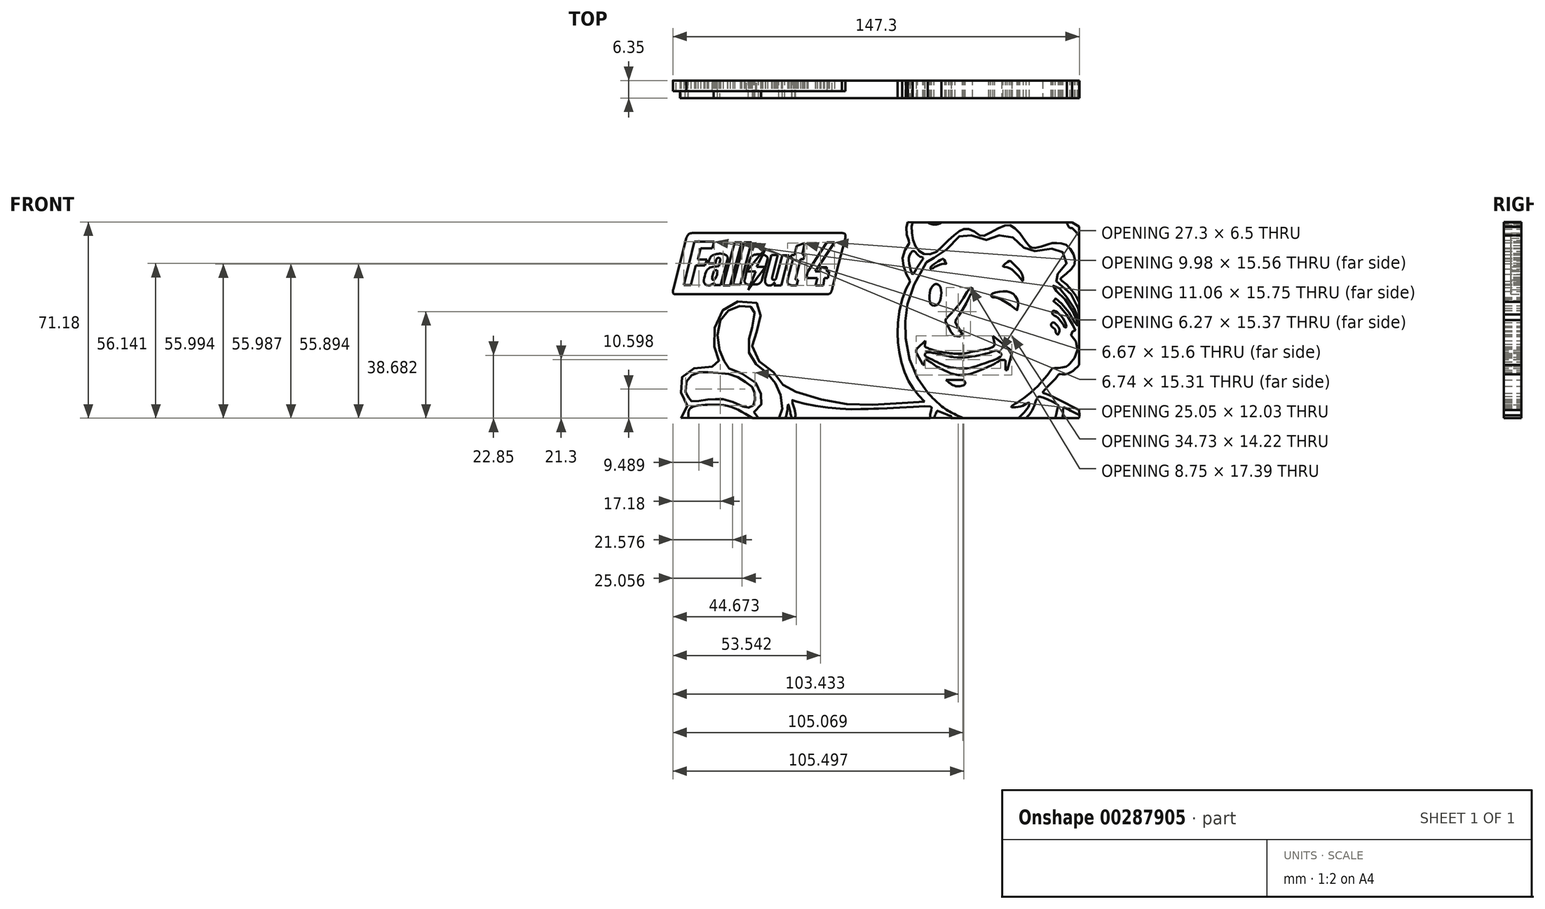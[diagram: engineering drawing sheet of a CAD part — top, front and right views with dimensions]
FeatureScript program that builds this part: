
annotation { "Feature Type Name" : "Feature", "Feature Type Description" : "" }
export const myFeature = defineFeature(function(context is Context, id is Id, definition is map)
    precondition{}
    {
        {
            var Q0;
            Q0=qCreatedBy(makeId("Front.planeOp"),FACE);
            var sketch = newSketch(context, id + "F0", { "sketchPlane" : qUnion([Q0])});
            skLineSegment(sketch, "E0", {"start": v(-63.85, 33.57) * mm, "end": v(-56.67, 33.57) * mm});
            skLineSegment(sketch, "E1", {"start": v(-56.67, 33.57) * mm, "end": v(-57.4, 31.22) * mm});
            skLineSegment(sketch, "E2", {"start": v(-57.4, 31.22) * mm, "end": v(-61.58, 31.22) * mm});
            skLineSegment(sketch, "E3", {"start": v(-61.58, 31.22) * mm, "end": v(-62.68, 27.12) * mm});
            skLineSegment(sketch, "E4", {"start": v(-62.68, 27.12) * mm, "end": v(-59.3, 27.12) * mm});
            skLineSegment(sketch, "E5", {"start": v(-59.3, 27.12) * mm, "end": v(-60.11, 24.92) * mm});
            skLineSegment(sketch, "E6", {"start": v(-60.11, 24.92) * mm, "end": v(-63.4, 24.92) * mm});
            skLineSegment(sketch, "E7", {"start": v(-63.4, 24.92) * mm, "end": v(-65.24, 17.82) * mm});
            skLineSegment(sketch, "E8", {"start": v(-65.24, 17.82) * mm, "end": v(-67.73, 17.82) * mm});
            skLineSegment(sketch, "E9", {"start": v(-67.73, 17.82) * mm, "end": v(-63.85, 33.57) * mm});
            skLineSegment(sketch, "E10", {"start": v(-49.34, 33.35) * mm, "end": v(-46.78, 33.35) * mm});
            skLineSegment(sketch, "E11", {"start": v(-46.78, 33.35) * mm, "end": v(-50.96, 17.74) * mm});
            skLineSegment(sketch, "E12", {"start": v(-50.96, 17.74) * mm, "end": v(-53.45, 17.74) * mm});
            skLineSegment(sketch, "E13", {"start": v(-53.45, 17.74) * mm, "end": v(-49.34, 33.35) * mm});
            skLineSegment(sketch, "E14", {"start": v(-45.9, 33.35) * mm, "end": v(-43.26, 33.35) * mm});
            skLineSegment(sketch, "E15", {"start": v(-43.26, 33.35) * mm, "end": v(-47.22, 18.04) * mm});
            skLineSegment(sketch, "E16", {"start": v(-47.22, 18.04) * mm, "end": v(-50, 18.04) * mm});
            skLineSegment(sketch, "E17", {"start": v(-50, 18.04) * mm, "end": v(-45.9, 33.35) * mm});
            skPoint(sketch, "E18.13.internal.orphan", {"position": v(-38.14, 18.1) * mm});
            skPoint(sketch, "E18.14.internal.orphan", {"position": v(-38.14, 20.67) * mm});
            skPoint(sketch, "E18.15.internal.orphan", {"position": v(-37.04, 24.48) * mm});
            skPoint(sketch, "E19.start.orphan", {"position": v(-23.14, 20.54) * mm});
            skPoint(sketch, "E20.start.orphan", {"position": v(-16.58, 20.54) * mm});
            skLineSegment(sketch, "E21", {"start": v(-35.93, 28.79) * mm, "end": v(-33.7, 28.79) * mm});
            skLineSegment(sketch, "E22", {"start": v(-33.7, 28.79) * mm, "end": v(-35.76, 20.65) * mm});
            skLineSegment(sketch, "E23", {"start": v(-29.6, 28.68) * mm, "end": v(-31.98, 28.68) * mm});
            skLineSegment(sketch, "E24", {"start": v(-31.98, 28.68) * mm, "end": v(-34.2, 20.7) * mm});
            skLineSegment(sketch, "E25", {"start": v(-35.93, 28.79) * mm, "end": v(-38.14, 20.67) * mm});
            skLineSegment(sketch, "E26", {"start": v(-29.6, 28.68) * mm, "end": v(-32.36, 17.79) * mm});
            skLineSegment(sketch, "E27", {"start": v(-32.36, 17.79) * mm, "end": v(-35.03, 17.79) * mm});
            skFitSpline(sketch, "E28", {"points": [v(-35.76, 20.65) * mm, v(-35.65, 19.94) * mm, v(-34.99, 19.79) * mm, v(-34.43, 20) * mm, v(-34.2, 20.7) * mm], "startDerivative": vector(-0.16, -3.28) * mm, "endDerivative": vector(0.54, 3.14) * mm});
            skLineSegment(sketch, "E29", {"start": v(-35.03, 17.79) * mm, "end": v(-34.72, 18.75) * mm});
            skFitSpline(sketch, "E30", {"points": [v(-34.72, 18.75) * mm, v(-34.94, 18.75) * mm, v(-35.56, 18.07) * mm, v(-37.05, 17.76) * mm, v(-38.15, 18.56) * mm, v(-38.14, 20.67) * mm], "startDerivative": vector(-2.4, 0.72) * mm, "endDerivative": vector(1.34, 8.58) * mm});
            skLineSegment(sketch, "E31", {"start": v(-23.88, 33.13) * mm, "end": v(-26.81, 32.04) * mm});
            skLineSegment(sketch, "E32", {"start": v(-26.81, 32.04) * mm, "end": v(-27.54, 28.79) * mm});
            skLineSegment(sketch, "E33", {"start": v(-27.54, 28.79) * mm, "end": v(-28.74, 28.79) * mm});
            skLineSegment(sketch, "E34", {"start": v(-28.74, 28.79) * mm, "end": v(-28.96, 27.47) * mm});
            skLineSegment(sketch, "E35", {"start": v(-28.96, 27.47) * mm, "end": v(-28.06, 27.47) * mm});
            skLineSegment(sketch, "E36", {"start": v(-28.06, 27.47) * mm, "end": v(-29.95, 20.3) * mm});
            skLineSegment(sketch, "E37", {"start": v(-23.88, 33.13) * mm, "end": v(-24.83, 28.97) * mm});
            skLineSegment(sketch, "E38", {"start": v(-24.83, 28.97) * mm, "end": v(-23.88, 28.97) * mm});
            skLineSegment(sketch, "E39", {"start": v(-23.88, 28.97) * mm, "end": v(-24.23, 27.33) * mm});
            skLineSegment(sketch, "E40", {"start": v(-24.23, 27.33) * mm, "end": v(-25.41, 27.33) * mm});
            skLineSegment(sketch, "E41", {"start": v(-25.41, 27.33) * mm, "end": v(-27.09, 20.63) * mm});
            skFitSpline(sketch, "E42", {"points": [v(-27.09, 20.63) * mm, v(-27.09, 19.84) * mm, v(-26.27, 19.84) * mm], "startDerivative": vector(-0.4, -2) * mm, "endDerivative": vector(2.04, 0.4) * mm});
            skLineSegment(sketch, "E43", {"start": v(-26.27, 19.84) * mm, "end": v(-26.8, 17.83) * mm});
            skFitSpline(sketch, "E44", {"points": [v(-29.95, 20.3) * mm, v(-30.1, 18.74) * mm, v(-29.18, 17.9) * mm, v(-26.8, 17.83) * mm], "startDerivative": vector(-1.34, -5.23) * mm, "endDerivative": vector(6.63, 0.57) * mm});
            skLineSegment(sketch, "E45", {"start": v(-15.88, 33.32) * mm, "end": v(-13.16, 33.32) * mm});
            skLineSegment(sketch, "E46", {"start": v(-13.16, 33.32) * mm, "end": v(-20.15, 22.87) * mm});
            skLineSegment(sketch, "E47", {"start": v(-20.15, 22.87) * mm, "end": v(-18.48, 22.87) * mm});
            skLineSegment(sketch, "E48", {"start": v(-18.48, 22.87) * mm, "end": v(-18.12, 24.37) * mm});
            skLineSegment(sketch, "E49", {"start": v(-18.12, 24.37) * mm, "end": v(-15.92, 24.37) * mm});
            skLineSegment(sketch, "E50", {"start": v(-15.92, 22.87) * mm, "end": v(-15.03, 22.87) * mm});
            skLineSegment(sketch, "E51", {"start": v(-15.03, 22.87) * mm, "end": v(-15.53, 20.37) * mm});
            skLineSegment(sketch, "E52", {"start": v(-15.53, 20.37) * mm, "end": v(-16.78, 20.37) * mm});
            skLineSegment(sketch, "E53", {"start": v(-16.78, 20.37) * mm, "end": v(-17.14, 17.76) * mm});
            skLineSegment(sketch, "E54", {"start": v(-17.14, 17.76) * mm, "end": v(-20, 17.76) * mm});
            skLineSegment(sketch, "E55", {"start": v(-20, 17.76) * mm, "end": v(-19.27, 20.37) * mm});
            skLineSegment(sketch, "E56", {"start": v(-19.27, 20.37) * mm, "end": v(-23.14, 20.37) * mm});
            skLineSegment(sketch, "E57", {"start": v(-23.14, 20.37) * mm, "end": v(-23.14, 21.57) * mm});
            skLineSegment(sketch, "E58", {"start": v(-22.78, 22.87) * mm, "end": v(-15.88, 33.32) * mm});
            skLineSegment(sketch, "E59", {"start": v(-22.78, 22.87) * mm, "end": v(-23.14, 21.57) * mm});
            skLineSegment(sketch, "E60", {"start": v(-15.92, 24.37) * mm, "end": v(-15.92, 22.87) * mm});
            skPoint(sketch, "E61.10.internal.orphan", {"position": v(-71.53, 16.13) * mm});
            skPoint(sketch, "E62.10.internal.orphan", {"position": v(-38.14, 28.8) * mm});
            skPoint(sketch, "E62.5.internal.orphan", {"position": v(-44.95, 18.18) * mm});
            skLineSegment(sketch, "E63", {"start": v(-54.48, 27.02) * mm, "end": v(-55, 24.67) * mm});
            skLineSegment(sketch, "E64", {"start": v(-52.02, 26.91) * mm, "end": v(-54.39, 17.91) * mm});
            skLineSegment(sketch, "E65", {"start": v(-54.39, 17.91) * mm, "end": v(-56.84, 17.91) * mm});
            skLineSegment(sketch, "E66", {"start": v(-56.84, 17.91) * mm, "end": v(-56.65, 18.62) * mm});
            skLineSegment(sketch, "E67", {"start": v(-56.26, 25.8) * mm, "end": v(-58.83, 25.8) * mm});
            skLineSegment(sketch, "E68", {"start": v(-56.26, 25.8) * mm, "end": v(-56.02, 26.9) * mm});
            skFitSpline(sketch, "E69", {"points": [v(-56.02, 26.9) * mm, v(-55.64, 27.6) * mm, v(-54.92, 27.7) * mm, v(-54.52, 27.38) * mm, v(-54.48, 27.02) * mm], "startDerivative": vector(0.9, 2.82) * mm, "endDerivative": vector(-0.12, -1.87) * mm});
            skFitSpline(sketch, "E70", {"points": [v(-58.83, 25.8) * mm, v(-58.07, 28) * mm, v(-57.05, 28.76) * mm, v(-55.57, 29.2) * mm, v(-53.5, 29.16) * mm, v(-51.91, 28.14) * mm, v(-52.02, 26.91) * mm], "startDerivative": vector(3.07, 12.97) * mm, "endDerivative": vector(-2.97, -9.05) * mm});
            skFitSpline(sketch, "E71", {"points": [v(-56.65, 18.62) * mm, v(-57.35, 18.23) * mm, v(-58.4, 17.73) * mm, v(-59.8, 17.98) * mm, v(-60.42, 18.86) * mm, v(-60.16, 21.18) * mm, v(-59.46, 23.12) * mm, v(-58.54, 24.03) * mm, v(-57.42, 24.5) * mm, v(-55, 24.67) * mm], "startDerivative": vector(-8.34, -4.38) * mm, "endDerivative": vector(18.81, 0.4) * mm});
            skFitSpline(sketch, "E72", {"points": [v(-55.8, 23.29) * mm, v(-56.65, 23.05) * mm, v(-57.18, 21.9) * mm, v(-57.48, 20.39) * mm, v(-57.29, 19.76) * mm, v(-56.65, 19.9) * mm, v(-56.1, 20.6) * mm, v(-55.6, 22.31) * mm, v(-55.8, 23.29) * mm]});
            skPoint(sketch, "E73.orphan", {"position": v(-38.14, 31) * mm});
            skPoint(sketch, "E74.end.orphan", {"position": v(-44.36, 16.13) * mm});
            skPoint(sketch, "E75.start.orphan", {"position": v(-44.95, 22.8) * mm});
            skPoint(sketch, "E76.2.internal.orphan", {"position": v(-43.57, 18.18) * mm});
            skPoint(sketch, "E77.start.orphan", {"position": v(-38.14, 24.48) * mm});
            skLineSegment(sketch, "E78", {"start": v(-44.95, 22.8) * mm, "end": v(-41.74, 22.8) * mm});
            skLineSegment(sketch, "E79", {"start": v(-41.74, 22.8) * mm, "end": v(-43.72, 17.78) * mm});
            skLineSegment(sketch, "E80", {"start": v(-41.35, 24.5) * mm, "end": v(-38.14, 24.48) * mm});
            skLineSegment(sketch, "E81", {"start": v(-38.14, 24.48) * mm, "end": v(-44.36, 16.13) * mm});
            skLineSegment(sketch, "E82", {"start": v(-43.72, 17.78) * mm, "end": v(-44.36, 16.13) * mm});
            skPoint(sketch, "E83.start.orphan", {"position": v(-38.14, 30.6) * mm});
            skLineSegment(sketch, "E84", {"start": v(-41.35, 24.5) * mm, "end": v(-38.14, 31) * mm});
            skLineSegment(sketch, "E85", {"start": v(-39.77, 29.18) * mm, "end": v(-44.95, 22.8) * mm});
            skLineSegment(sketch, "E86", {"start": v(-39.77, 29.18) * mm, "end": v(-38.14, 31) * mm});
            skLineSegment(sketch, "E87", {"start": v(-44.95, 22.8) * mm, "end": v(-43.87, 27) * mm});
            skFitSpline(sketch, "E88", {"points": [v(-43.87, 27) * mm, v(-43.47, 27.97) * mm, v(-42.78, 28.55) * mm, v(-41.95, 28.9) * mm, v(-40.62, 29.08) * mm, v(-39.85, 29.07) * mm], "startDerivative": vector(1.5, 5.13) * mm, "endDerivative": vector(3.94, -0.22) * mm});
            skLineSegment(sketch, "E89", {"start": v(-38.14, 24.48) * mm, "end": v(-37.38, 27.31) * mm});
            skFitSpline(sketch, "E90", {"points": [v(-37.38, 27.31) * mm, v(-37.38, 27.8) * mm, v(-37.74, 28.26) * mm, v(-38.35, 28.69) * mm, v(-39.15, 28.96) * mm], "startDerivative": vector(0.35, 2.35) * mm, "endDerivative": vector(-2.93, 0.81) * mm});
            skLineSegment(sketch, "E91", {"start": v(-38.14, 24.48) * mm, "end": v(-39.5, 19.4) * mm});
            skFitSpline(sketch, "E92", {"points": [v(-39.5, 19.4) * mm, v(-40.02, 18.78) * mm, v(-40.6, 18.3) * mm, v(-41.79, 18.1) * mm, v(-42.9, 18.1) * mm], "startDerivative": vector(-2.27, -2.74) * mm, "endDerivative": vector(-3.97, 0.04) * mm});
            skLineSegment(sketch, "E93", {"start": v(-44.95, 22.8) * mm, "end": v(-45.68, 19.95) * mm});
            skFitSpline(sketch, "E94", {"points": [v(-45.68, 19.95) * mm, v(-45.68, 18.94) * mm, v(-44.95, 18.18) * mm, v(-43.6, 18.06) * mm], "startDerivative": vector(-0.5, -3.29) * mm, "endDerivative": vector(3.92, 0.17) * mm});
            skSolve(sketch);
        }
        {
            var Q0;
            Q0=qCreatedBy(makeId("Front.planeOp"),FACE);
            var sketch = newSketch(context, id + "F1", { "sketchPlane" : qUnion([Q0])});
            skLineSegment(sketch, "E95", {"start": v(-63.81, 36.77) * mm, "end": v(-12.41, 36.77) * mm});
            skLineSegment(sketch, "E96", {"start": v(-9.4, 34.04) * mm, "end": v(-13.7, 17.53) * mm});
            skLineSegment(sketch, "E97", {"start": v(-17.3, 14.51) * mm, "end": v(-68.84, 14.51) * mm});
            skLineSegment(sketch, "E98", {"start": v(-66.83, 34.9) * mm, "end": v(-71.57, 16.38) * mm});
            skFitSpline(sketch, "E99", {"points": [v(-66.83, 34.9) * mm, v(-65.9, 36.4) * mm, v(-63.81, 36.77) * mm], "startDerivative": vector(1.47, 3.75) * mm, "endDerivative": vector(4.51, 0.04) * mm});
            skLineSegment(sketch, "E100", {"start": v(-68.84, 14.51) * mm, "end": v(-70.55, 14.51) * mm});
            skFitSpline(sketch, "E101", {"points": [v(-70.55, 14.51) * mm, v(-71.44, 14.72) * mm, v(-71.69, 15.6) * mm, v(-71.57, 16.38) * mm], "startDerivative": vector(-3.02, 0.07) * mm, "endDerivative": vector(0.56, 2.28) * mm});
            skLineSegment(sketch, "E102", {"start": v(-17.3, 14.51) * mm, "end": v(-15.8, 14.51) * mm});
            skLineSegment(sketch, "E103", {"start": v(-13.7, 17.53) * mm, "end": v(-14.05, 16.18) * mm});
            skFitSpline(sketch, "E104", {"points": [v(-14.05, 16.18) * mm, v(-14.63, 14.9) * mm, v(-15.8, 14.51) * mm], "startDerivative": vector(-0.8, -2.88) * mm, "endDerivative": vector(-2.72, -0.42) * mm});
            skLineSegment(sketch, "E105", {"start": v(-12.41, 36.77) * mm, "end": v(-10.38, 36.77) * mm});
            skFitSpline(sketch, "E106", {"points": [v(-9.4, 34.04) * mm, v(-9.14, 35.44) * mm, v(-9.4, 36.48) * mm, v(-10.38, 36.77) * mm], "startDerivative": vector(0.97, 3.8) * mm, "endDerivative": vector(-3.67, 0.34) * mm});
            skSolve(sketch);
        }
        {
            var Q0;
            Q0 = qSketchRegion(id + "F1", true);
            extrude(context, id + "F2", {"entities" : qUnion([Q0]), "depth" : 3.8 * mm});
        }
        {
            var Q0;
            Q0 = qSketchRegion(id + "F0", true);
            extrude(context, id + "F3", {"entities" : qUnion([Q0]), "operationType" : NewBodyOperationType.REMOVE, "oppositeDirection" : true, "depth" : 50.8 * mm, "hasSecondDirection" : true, "secondDirectionOppositeDirection" : false, "secondDirectionDepth" : 50.8 * mm});
        }
        {
            var Q0;
            {var subQ0=sQuery(id+"F0.wireOp",EDGE,"E87");Q0=makeQuery(id+"F0.imprint","IMPRINT",FACE,{"disambiguationData":[TD([[makeQuery(id+"F0.imprint","IMPRINT",EDGE,{"derivedFrom":subQ0}),-1.0]])]});}
            var Q1;
            {var subQ0=sQuery(id+"F0.wireOp",EDGE,"E80");Q1=makeQuery(id+"F0.imprint","IMPRINT",FACE,{"disambiguationData":[TD([[makeQuery(id+"F0.imprint","IMPRINT",EDGE,{"derivedFrom":subQ0}),1.0]])]});}
            var Q2;
            {var subQ0=sQuery(id+"F0.wireOp",EDGE,"E78");Q2=makeQuery(id+"F0.imprint","IMPRINT",FACE,{"disambiguationData":[TD([[makeQuery(id+"F0.imprint","IMPRINT",EDGE,{"derivedFrom":subQ0}),-1.0]])]});}
            var Q3;
            {var subQ0=sQuery(id+"F0.wireOp",EDGE,"E91");Q3=makeQuery(id+"F0.imprint","IMPRINT",FACE,{"disambiguationData":[TD([[makeQuery(id+"F0.imprint","IMPRINT",EDGE,{"derivedFrom":subQ0}),-1.0]])]});}
            extrude(context, id + "F4", {"entities" : qUnion([Q0, Q1, Q2, Q3]), "depth" : 3.8 * mm});
        }
        {
            var Q0;
            Q0=qCreatedBy(makeId("Front.planeOp"),FACE);
            var sketch = newSketch(context, id + "F5", { "sketchPlane" : qUnion([Q0])});
            skFitSpline(sketch, "E107", {"points": [v(-68.68, -30.34) * mm, v(-68.33, -27.94) * mm, v(-66.38, -25.59) * mm, v(-67.92, -23.03) * mm, v(-69.04, -19.55) * mm, v(-68.63, -16.07) * mm, v(-66.9, -13.82) * mm, v(-64.03, -12.3) * mm, v(-59.02, -11.68) * mm, v(-55.85, -11.68) * mm, v(-54.73, -10.65) * mm, v(-55.34, -8.81) * mm, v(-56.36, -5.75) * mm, v(-56.87, -1.96) * mm, v(-56.26, 3.77) * mm, v(-54.01, 8.27) * mm, v(-50.64, 11.13) * mm, v(-46.03, 12.15) * mm, v(-41.23, 11.33) * mm, v(-40, 9.29) * mm, v(-39.9, 6.32) * mm, v(-40.82, 2.64) * mm, v(-42.15, -1.04) * mm, v(-42.97, -3.6) * mm, v(-41.64, -8.3) * mm, v(-39.7, -10.35) * mm, v(-35.6, -13.42) * mm, v(-32.84, -16.18) * mm, v(-31.72, -18.53) * mm, v(-31.4, -18.84) * mm, v(-26.8, -20.98) * mm, v(-17.2, -23.85) * mm, v(-8.3, -25.38) * mm, v(1.11, -25.59) * mm, v(13.08, -24.87) * mm, v(19.52, -24.46) * mm], "startDerivative": vector(-9.45, 112.44) * mm, "endDerivative": vector(162.37, 9.81) * mm});
            skFitSpline(sketch, "E108", {"points": [v(19.52, -24.46) * mm, v(15.37, -19.6) * mm, v(12, -12.77) * mm, v(10, -3.93) * mm, v(9.9, 4.17) * mm, v(12.45, 15.65) * mm, v(14.36, 19.57) * mm, v(14.02, 19.83) * mm, v(12.12, 23.96) * mm, v(11.87, 29.38) * mm, v(14.19, 33.5) * mm, v(13.76, 34.02) * mm, v(12.81, 38.06) * mm, v(13.41, 40.73) * mm], "startDerivative": vector(-49.03, 51.65) * mm, "endDerivative": vector(15.36, 39.31) * mm});
            skFitSpline(sketch, "E109", {"points": [v(73.02, 40.63) * mm, v(75.51, 39.11) * mm], "startDerivative": vector(2.5, -1.52) * mm, "endDerivative": vector(2.5, -1.52) * mm});
            skFitSpline(sketch, "E110", {"points": [v(75.51, -11.1) * mm, v(73.4, -13.16) * mm, v(70.34, -14.47) * mm, v(68.27, -14.47) * mm, v(67.35, -15.7) * mm, v(62.37, -20.98) * mm, v(62.91, -21.36) * mm, v(75.51, -27.49) * mm], "startDerivative": vector(-14.96, -17) * mm, "endDerivative": vector(58.28, -29.89) * mm});
            skFitSpline(sketch, "E111", {"points": [v(-66, -30.3) * mm, v(-65.9, -27.49) * mm, v(-64.5, -26.28) * mm, v(-58.1, -25.52) * mm, v(-50.73, -26.28) * mm, v(-42.82, -30.4) * mm], "startDerivative": vector(-1.53, 21.1) * mm, "endDerivative": vector(29.91, -18.64) * mm});
            skFitSpline(sketch, "E112", {"points": [v(-40.64, -30.38) * mm, v(-42.46, -28.37) * mm, v(-42.1, -28.1) * mm, v(-39.64, -25.28) * mm, v(-39.64, -22) * mm, v(-41.46, -17.71) * mm, v(-48.2, -13.52) * mm, v(-52.12, -11.8) * mm, v(-53.12, -9.51) * mm, v(-54.85, -5.5) * mm, v(-55.4, 1.6) * mm, v(-53.3, 7.07) * mm, v(-49.57, 9.62) * mm, v(-45.29, 10.35) * mm, v(-42.55, 9.53) * mm, v(-42.1, 8.25) * mm, v(-43.1, 2.15) * mm, v(-44.1, -1.95) * mm, v(-43.83, -7.78) * mm, v(-40.18, -11.97) * mm, v(-36, -15.7) * mm, v(-33.35, -20.17) * mm, v(-31.98, -25.37) * mm, v(-32.8, -29.74) * mm, v(-33.26, -30.38) * mm], "startDerivative": vector(-79.5, 75.35) * mm, "endDerivative": vector(-24.05, -24.57) * mm});
            skFitSpline(sketch, "E113", {"points": [v(-31.4, -30.53) * mm, v(-30.65, -29.74) * mm, v(-29.88, -25.49) * mm, v(-29.4, -27.3) * mm, v(-28.55, -30.4) * mm], "startDerivative": vector(4.95, 2.02) * mm, "endDerivative": vector(3.13, -10.02) * mm});
            skFitSpline(sketch, "E114", {"points": [v(-64.91, -24.35) * mm, v(-60.79, -23.88) * mm, v(-56.43, -23.53) * mm, v(-51.72, -23.94) * mm, v(-45.06, -26.65) * mm, v(-44, -26.53) * mm, v(-42.3, -25.41) * mm, v(-41.94, -22.76) * mm, v(-42.4, -19.93) * mm, v(-45.6, -17.1) * mm, v(-50.9, -14.45) * mm, v(-58.26, -13.87) * mm, v(-63.32, -13.98) * mm, v(-66.56, -16.87) * mm, v(-66.97, -18.84) * mm, v(-67.1, -20.98) * mm, v(-65.85, -23.23) * mm, v(-64.91, -24.35) * mm]});
            skFitSpline(sketch, "E115", {"points": [v(-27.42, -30.4) * mm, v(-27.25, -28.71) * mm, v(-28.53, -24.02) * mm, v(-27.33, -24.24) * mm, v(-11.4, -26.99) * mm, v(0, -27.02) * mm, v(4.79, -26.92) * mm, v(21.57, -26.2) * mm, v(21.84, -26.38) * mm, v(22.11, -26.65) * mm, v(21.63, -28.3) * mm, v(21.56, -30.4) * mm], "startDerivative": vector(8.2, 21.52) * mm, "endDerivative": vector(3, -31.74) * mm});
            skFitSpline(sketch, "E116", {"points": [v(22.99, -30.32) * mm, v(24.15, -27.74) * mm, v(24.7, -27.91) * mm, v(29.13, -29.72) * mm, v(29.18, -29.8) * mm, v(29, -30.36) * mm], "startDerivative": vector(4.51, 12.02) * mm, "endDerivative": vector(-1.67, -5.2) * mm});
            skFitSpline(sketch, "E117", {"points": [v(66.9, -30.35) * mm, v(68, -25.83) * mm, v(67.97, -25.64) * mm, v(61.19, -22.53) * mm, v(60.65, -22.8) * mm, v(60.08, -23.5) * mm, v(59.54, -25.3) * mm, v(58.12, -28.2) * mm, v(56.36, -30.42) * mm], "startDerivative": vector(7.82, 33.75) * mm, "endDerivative": vector(-12.8, -14.65) * mm});
            skFitSpline(sketch, "E118", {"points": [v(75.6, -29.31) * mm, v(70.13, -26.51) * mm, v(70.05, -26.51) * mm, v(69.72, -27.24) * mm, v(69.68, -29.31) * mm, v(69.28, -30.45) * mm], "startDerivative": vector(-19.13, 9.91) * mm, "endDerivative": vector(-3, -5.65) * mm});
            skFitSpline(sketch, "E119", {"points": [v(33.9, -30.45) * mm, v(29.65, -28.58) * mm, v(25.47, -25.88) * mm, v(20.83, -21.43) * mm], "startDerivative": vector(-13.82, 5.6) * mm, "endDerivative": vector(-12.63, 13.03) * mm});
            skFitSpline(sketch, "E120", {"points": [v(20.83, -21.43) * mm, v(17.6, -16.99) * mm, v(14.9, -11.5) * mm, v(12.9, -3.9) * mm, v(12.58, 1.63) * mm, v(12.66, 5.95) * mm, v(13.26, 10.63) * mm, v(15.09, 16.65) * mm, v(20.01, 25.83) * mm, v(21.3, 27.62) * mm, v(21.53, 27.62) * mm, v(23.81, 28.12) * mm, v(26.68, 30.08) * mm, v(30.69, 34.04) * mm, v(33.29, 36.4) * mm, v(35.8, 36.27) * mm, v(39.3, 34.4) * mm, v(43.21, 34.5) * mm, v(46.04, 35.73) * mm, v(47.9, 36.05) * mm, v(51.69, 35.05) * mm, v(54.83, 32.45) * mm, v(56.01, 30.76) * mm, v(57.96, 30.1) * mm, v(62.94, 30.84) * mm, v(66.29, 31.05) * mm, v(68.47, 30.73) * mm, v(70.2, 29) * mm, v(71.02, 26.9) * mm, v(70.52, 24.45) * mm, v(68.1, 22.08) * mm, v(66.28, 20.94) * mm, v(66.55, 19.85) * mm, v(70.15, 17.07) * mm, v(74.34, 11.97) * mm, v(75.13, 9.54) * mm], "startDerivative": vector(-94.55, 122.24) * mm, "endDerivative": vector(18.57, -91.09) * mm});
            skFitSpline(sketch, "E121", {"points": [v(75.13, 9.54) * mm, v(75.57, 7.15) * mm], "startDerivative": vector(0.43, -2.4) * mm, "endDerivative": vector(0.43, -2.4) * mm});
            skFitSpline(sketch, "E122", {"points": [v(75.54, 5.23) * mm, v(73.01, 10.67) * mm, v(69.97, 14.93) * mm, v(67.39, 17.67) * mm, v(66.17, 17.67) * mm, v(66.17, 16.78) * mm, v(68.27, 14.9) * mm, v(72.16, 10.28) * mm, v(74.29, 5.93) * mm, v(74.98, 4.38) * mm, v(74.98, 3.44) * mm, v(74.6, 2.95) * mm, v(74.02, 3.98) * mm, v(72.16, 7.6) * mm, v(69.24, 11.16) * mm, v(67.33, 12.83) * mm, v(66.57, 13.1) * mm, v(66.08, 12.74) * mm, v(66.69, 11.52) * mm, v(68.8, 9.86) * mm, v(71.15, 6.9) * mm, v(73.64, 2.74) * mm, v(74.05, 1.95) * mm, v(74.02, 1.37) * mm, v(73.15, 1.34) * mm, v(73.24, 1.05) * mm, v(72.34, 0.95) * mm, v(72.4, 0) * mm, v(73.85, -1.6) * mm, v(74.74, -3.74) * mm, v(74.74, -6.51) * mm, v(73.9, -8.54) * mm], "startDerivative": vector(-42.47, 103.93) * mm, "endDerivative": vector(-30.71, -57.47) * mm});
            skFitSpline(sketch, "E123", {"points": [v(73.9, -8.54) * mm, v(72.4, -10.37) * mm, v(70.34, -11.82) * mm, v(65.67, -12.4) * mm, v(65.6, -12.54) * mm, v(61.62, -17.6) * mm, v(54.97, -23.53) * mm, v(51.36, -25.77) * mm], "startDerivative": vector(-13.26, -16.22) * mm, "endDerivative": vector(-21.89, -12.39) * mm});
            skFitSpline(sketch, "E124", {"points": [v(51.36, -25.77) * mm, v(50.96, -26.26) * mm, v(51.36, -26.47) * mm, v(55.32, -25.77) * mm, v(57.4, -24.83) * mm, v(57.2, -26.16) * mm, v(53.52, -30.4) * mm], "startDerivative": vector(-6.4, -5.89) * mm, "endDerivative": vector(-16.44, -15.88) * mm});
            skFitSpline(sketch, "E125", {"points": [v(65.37, 3.22) * mm, v(66.82, 1.82) * mm, v(67.15, 0.52) * mm, v(67.88, 0) * mm, v(68.31, 1) * mm, v(68.31, 2.16) * mm, v(66.59, 4.14) * mm, v(65.8, 4.24) * mm, v(65.37, 3.22) * mm]});
            skFitSpline(sketch, "E126", {"points": [v(68.06, 5.76) * mm, v(69.3, 4.3) * mm, v(70.5, 2.55) * mm, v(70.82, 2.55) * mm, v(70.84, 3.5) * mm, v(69.3, 6.3) * mm, v(67.06, 8.37) * mm, v(66, 8.43) * mm, v(65.8, 7.51) * mm, v(67.51, 6.25) * mm, v(68.06, 5.76) * mm]});
            skFitSpline(sketch, "E127", {"points": [v(19.07, 27.84) * mm, v(16.98, 24.58) * mm, v(15.31, 21.84) * mm, v(14.16, 24.66) * mm, v(13.94, 28.13) * mm, v(15.31, 30.23) * mm, v(16.47, 29.57) * mm, v(17.7, 28.27) * mm, v(19.07, 27.84) * mm]});
            skFitSpline(sketch, "E128", {"points": [v(15.27, 40.58) * mm, v(14.84, 39.55) * mm, v(15, 36.08) * mm, v(15.98, 32.45) * mm, v(17.76, 29.96) * mm, v(19.88, 29.04) * mm, v(23.23, 29.58) * mm, v(27.14, 33.05) * mm, v(30.5, 36.24) * mm, v(32.93, 37.87) * mm, v(34.61, 38.25) * mm, v(36.94, 37.6) * mm, v(39.76, 35.8) * mm, v(41.33, 35.8) * mm, v(45.99, 38.3) * mm, v(49.46, 39.65) * mm, v(51.46, 39.17) * mm, v(54.06, 36.62) * mm], "startDerivative": vector(-14.62, -23.8) * mm, "endDerivative": vector(40.67, -46.63) * mm});
            skFitSpline(sketch, "E129", {"points": [v(54.06, 36.62) * mm, v(57.98, 31.63) * mm, v(58.21, 31.57) * mm, v(58.63, 31.36) * mm, v(62.75, 32.14) * mm, v(65.88, 33.07) * mm, v(68.13, 33.14) * mm, v(71.03, 32.34) * mm, v(73.45, 29.1) * mm, v(74.03, 26.01) * mm, v(72.24, 23.17) * mm, v(68.86, 20.41) * mm, v(68.77, 20.32) * mm, v(68.91, 19.7) * mm, v(69.68, 19.26) * mm, v(74.03, 14.53) * mm, v(75.04, 12.64) * mm], "startDerivative": vector(49.5, -68.91) * mm, "endDerivative": vector(10.4, -25.67) * mm});
            skFitSpline(sketch, "E130", {"points": [v(75.04, 12.64) * mm, v(75.6, 11.76) * mm], "startDerivative": vector(0.56, -0.88) * mm, "endDerivative": vector(0.56, -0.88) * mm});
            skFitSpline(sketch, "E131", {"points": [v(71.05, 40.61) * mm, v(71.56, 39.28) * mm, v(72.28, 38.62) * mm, v(73.15, 38.36) * mm, v(75.35, 36) * mm, v(75.6, 35.9) * mm], "startDerivative": vector(1.9, -6.47) * mm, "endDerivative": vector(1.99, -0.04) * mm});
            skFitSpline(sketch, "E132", {"points": [v(20.71, 40.55) * mm, v(22.1, 39.97) * mm, v(24.29, 39.97) * mm, v(25.67, 40.55) * mm], "startDerivative": vector(4.01, -2.2) * mm, "endDerivative": vector(4.01, 2.2) * mm});
            skFitSpline(sketch, "E133", {"points": [v(26.28, 27.39) * mm, v(27.34, 25.72) * mm, v(27.34, 25.58) * mm, v(25.36, 25.4) * mm, v(21.91, 23.77) * mm, v(21.57, 23.9) * mm, v(23.14, 25.65) * mm, v(25.8, 27.25) * mm, v(26.28, 27.39) * mm]});
            skFitSpline(sketch, "E134", {"points": [v(48.13, 25) * mm, v(50.22, 26.66) * mm, v(51.26, 26.03) * mm, v(55.07, 21.35) * mm, v(55.07, 19.34) * mm, v(54.67, 19.77) * mm, v(52.52, 22.3) * mm, v(50.08, 24.1) * mm, v(47.96, 24.68) * mm, v(48.13, 25) * mm]});
            skFitSpline(sketch, "E135", {"points": [v(43.6, 14.33) * mm, v(44.02, 13.53) * mm, v(44.89, 13.46) * mm, v(49.4, 11.43) * mm, v(53.1, 8.73) * mm, v(53.07, 8.86) * mm, v(53.52, 10.76) * mm, v(52.55, 13.66) * mm, v(50.04, 15.46) * mm, v(45.72, 15.3) * mm, v(43.6, 14.33) * mm]});
            skFitSpline(sketch, "E136", {"points": [v(22.96, 18.02) * mm, v(21.84, 16.6) * mm, v(21.32, 14.02) * mm, v(21.67, 11.14) * mm, v(23.17, 10.33) * mm, v(24.9, 11.62) * mm, v(25.58, 14.37) * mm, v(25.32, 16.86) * mm, v(24.5, 18.02) * mm, v(23.6, 18.24) * mm, v(22.96, 18.02) * mm]});
            skFitSpline(sketch, "E137", {"points": [v(36.12, 16.93) * mm, v(34, 13.79) * mm, v(31.4, 10.07) * mm, v(27.39, 5.68) * mm, v(26.95, 4.86) * mm, v(28.1, 2.98) * mm, v(29.56, 0) * mm, v(31.68, -0.84) * mm, v(33.23, 0) * mm, v(32.4, 1.34) * mm, v(31, 3.75) * mm, v(30.62, 4.67) * mm, v(31, 5.53) * mm, v(33.47, 9.2) * mm, v(36.02, 14.08) * mm, v(36.94, 16.2) * mm, v(36.84, 16.83) * mm, v(36.12, 16.93) * mm]});
            skLineSegment(sketch, "E138", {"start": v(27.32, -16.53) * mm, "end": v(33.46, -16.53) * mm});
            skFitSpline(sketch, "E139", {"points": [v(27.32, -16.53) * mm, v(27.8, -16.99) * mm, v(30.06, -18.54) * mm, v(33.22, -18.66) * mm, v(34.31, -17.63) * mm, v(33.46, -16.53) * mm], "startDerivative": vector(3.22, -3.07) * mm, "endDerivative": vector(-7.24, 6.1) * mm});
            skFitSpline(sketch, "E140", {"points": [v(29.56, -6.95) * mm, v(26.32, -6.54) * mm, v(22.64, -5.72) * mm, v(19.7, -4.5) * mm], "startDerivative": vector(-9.67, 1.08) * mm, "endDerivative": vector(-8.7, 4.12) * mm});
            skFitSpline(sketch, "E141", {"points": [v(29.56, -6.95) * mm, v(33.46, -6.95) * mm, v(38.13, -6.06) * mm, v(44.27, -4.56) * mm, v(44.96, -3.54) * mm], "startDerivative": vector(15.52, -0.77) * mm, "endDerivative": vector(2.28, 7.58) * mm});
            skLineSegment(sketch, "E142", {"start": v(19.77, -2.27) * mm, "end": v(19.7, -4.5) * mm});
            skLineSegment(sketch, "E143", {"start": v(19.77, -2.27) * mm, "end": v(16.94, -5) * mm});
            skLineSegment(sketch, "E144", {"start": v(44.96, -3.54) * mm, "end": v(44.34, -0.49) * mm});
            skLineSegment(sketch, "E145", {"start": v(44.34, -0.49) * mm, "end": v(50.22, -5.32) * mm});
            skFitSpline(sketch, "E146", {"points": [v(50.22, -5.32) * mm, v(51.13, -6.32) * mm, v(51.04, -7.41) * mm], "startDerivative": vector(2.24, -1.8) * mm, "endDerivative": vector(-0.65, -2.4) * mm});
            skLineSegment(sketch, "E147", {"start": v(51.04, -7.41) * mm, "end": v(49.49, -12.92) * mm});
            skFitSpline(sketch, "E148", {"points": [v(49.49, -12.92) * mm, v(48.87, -12.92) * mm], "startDerivative": vector(-0.62, 0) * mm, "endDerivative": vector(-0.62, 0) * mm});
            skLineSegment(sketch, "E149", {"start": v(48.87, -12.92) * mm, "end": v(48.87, -10.02) * mm});
            skFitSpline(sketch, "E150", {"points": [v(48.87, -10.02) * mm, v(48.61, -9.42) * mm, v(47.1, -9.28) * mm, v(47, -9.32) * mm, v(45.6, -10.26) * mm, v(42.93, -11.65) * mm], "startDerivative": vector(-0.14, 4.65) * mm, "endDerivative": vector(-8.43, -4.08) * mm});
            skFitSpline(sketch, "E151", {"points": [v(42.93, -11.65) * mm, v(39.77, -13) * mm, v(35.32, -14.48) * mm, v(30.87, -14.61) * mm, v(28.45, -13.94) * mm], "startDerivative": vector(-12.6, -5.47) * mm, "endDerivative": vector(-10.75, 3.88) * mm});
            skFitSpline(sketch, "E152", {"points": [v(28.45, -13.94) * mm, v(23.87, -11.65) * mm, v(21.55, -10.02) * mm, v(20.77, -9.57) * mm, v(20.32, -9.25) * mm, v(19.74, -9.4) * mm, v(19.54, -10.02) * mm, v(19.47, -11.01) * mm, v(18.92, -10.94) * mm], "startDerivative": vector(-19.47, 8.72) * mm, "endDerivative": vector(-8.06, 3.23) * mm});
            skLineSegment(sketch, "E153", {"start": v(18.92, -10.94) * mm, "end": v(16.8, -7.03) * mm});
            skFitSpline(sketch, "E154", {"points": [v(16.8, -7.03) * mm, v(16.46, -6.33) * mm, v(16.53, -5.66) * mm, v(16.94, -5) * mm], "startDerivative": vector(-1.26, 2.03) * mm, "endDerivative": vector(1.38, 1.9) * mm});
            skFitSpline(sketch, "E155", {"points": [v(28.25, -7.93) * mm, v(24.04, -7.02) * mm, v(21.48, -6.54) * mm, v(20.08, -6.54) * mm, v(19.74, -7.03) * mm, v(19.74, -7.8) * mm, v(20.64, -8.46) * mm], "startDerivative": vector(-16.27, 3.57) * mm, "endDerivative": vector(8.17, -4.14) * mm});
            skFitSpline(sketch, "E156", {"points": [v(20.64, -8.46) * mm, v(23.7, -9.92) * mm, v(27.62, -11.63) * mm, v(31.56, -12.3) * mm, v(35.37, -12.3) * mm, v(39.84, -11) * mm, v(42.73, -10) * mm], "startDerivative": vector(18.99, -8.82) * mm, "endDerivative": vector(18.15, 6.17) * mm});
            skFitSpline(sketch, "E157", {"points": [v(42.73, -10) * mm, v(47, -8.15) * mm, v(47.41, -7.41) * mm, v(47, -6.54) * mm, v(45.95, -6.07) * mm, v(45.26, -5.9) * mm, v(43.35, -6.54) * mm, v(40.18, -7.41) * mm, v(36.8, -8.06) * mm, v(33.46, -8.46) * mm, v(29.8, -8.24) * mm, v(28.25, -7.93) * mm], "startDerivative": vector(39.66, 14.38) * mm, "endDerivative": vector(-17.39, 4.25) * mm});
            skLineSegment(sketch, "E158", {"start": v(-33.11, -30.23) * mm, "end": v(-33.12, -30.23) * mm});
            skLineSegment(sketch, "E159", {"start": v(-42.82, -30.4) * mm, "end": v(-66, -30.3) * mm});
            skLineSegment(sketch, "E160", {"start": v(29, -30.36) * mm, "end": v(22.99, -30.32) * mm});
            skLineSegment(sketch, "E161", {"start": v(56.36, -30.42) * mm, "end": v(66.9, -30.35) * mm});
            skLineSegment(sketch, "E162", {"start": v(69.03, -30.4) * mm, "end": v(75.56, -30.42) * mm});
            skLineSegment(sketch, "E163", {"start": v(75.56, -30.42) * mm, "end": v(75.6, -29.31) * mm});
            skLineSegment(sketch, "E164", {"start": v(75.51, -27.49) * mm, "end": v(75.6, -29.31) * mm});
            skLineSegment(sketch, "E165", {"start": v(75.51, -27.49) * mm, "end": v(75.51, -11.1) * mm});
            skLineSegment(sketch, "E166", {"start": v(69.28, -30.45) * mm, "end": v(66.9, -30.35) * mm});
            skLineSegment(sketch, "E167", {"start": v(56.36, -30.42) * mm, "end": v(53.52, -30.4) * mm});
            skLineSegment(sketch, "E168", {"start": v(53.52, -30.4) * mm, "end": v(33.9, -30.45) * mm});
            skLineSegment(sketch, "E169", {"start": v(33.9, -30.45) * mm, "end": v(29, -30.36) * mm});
            skLineSegment(sketch, "E170", {"start": v(22.99, -30.32) * mm, "end": v(21.56, -30.4) * mm});
            skLineSegment(sketch, "E171", {"start": v(21.56, -30.4) * mm, "end": v(-27.42, -30.4) * mm});
            skLineSegment(sketch, "E172", {"start": v(-27.42, -30.4) * mm, "end": v(-28.55, -30.4) * mm});
            skLineSegment(sketch, "E173", {"start": v(-66, -30.3) * mm, "end": v(-68.68, -30.34) * mm});
            skLineSegment(sketch, "E174", {"start": v(75.51, -11.1) * mm, "end": v(75.54, 5.23) * mm});
            skLineSegment(sketch, "E175", {"start": v(75.54, 5.23) * mm, "end": v(75.57, 7.15) * mm});
            skLineSegment(sketch, "E176", {"start": v(75.57, 7.15) * mm, "end": v(75.6, 11.76) * mm});
            skLineSegment(sketch, "E177", {"start": v(75.6, 11.76) * mm, "end": v(75.6, 35.9) * mm});
            skLineSegment(sketch, "E178", {"start": v(75.6, 35.9) * mm, "end": v(75.6, 39) * mm});
            skLineSegment(sketch, "E179", {"start": v(75.6, 39) * mm, "end": v(75.51, 39.11) * mm});
            skLineSegment(sketch, "E180", {"start": v(73.02, 40.63) * mm, "end": v(71.05, 40.61) * mm});
            skLineSegment(sketch, "E181", {"start": v(71.05, 40.61) * mm, "end": v(25.67, 40.55) * mm});
            skLineSegment(sketch, "E182", {"start": v(20.71, 40.55) * mm, "end": v(15.27, 40.58) * mm});
            skLineSegment(sketch, "E183", {"start": v(20.71, 40.55) * mm, "end": v(25.67, 40.55) * mm});
            skLineSegment(sketch, "E184", {"start": v(15.27, 40.58) * mm, "end": v(13.41, 40.73) * mm});
            skLineSegment(sketch, "E185", {"start": v(73.02, 40.63) * mm, "end": v(75.51, 40.62) * mm});
            skLineSegment(sketch, "E186", {"start": v(75.51, 40.62) * mm, "end": v(75.6, 39) * mm});
            skLineSegment(sketch, "E187", {"start": v(-31.16, -30.41) * mm, "end": v(-28.55, -30.4) * mm});
            skLineSegment(sketch, "E188", {"start": v(-40.64, -30.38) * mm, "end": v(-33.26, -30.38) * mm});
            skLineSegment(sketch, "E189", {"start": v(-31.16, -30.41) * mm, "end": v(-33.26, -30.38) * mm});
            skLineSegment(sketch, "E190", {"start": v(-40.64, -30.38) * mm, "end": v(-42.82, -30.4) * mm});
            skSolve(sketch);
        }
        {
            var Q0;
            Q0=sQuery(id+"F5.wireOp",EDGE,"E107");
            var Q1;
            Q1=sQuery(id+"F5.wireOp",EDGE,"E108");
            var Q2;
            Q2=sQuery(id+"F5.wireOp",EDGE,"E131");
            var Q3;
            Q3=sQuery(id+"F5.wireOp",EDGE,"E109");
            var Q4;
            Q4=sQuery(id+"F5.wireOp",EDGE,"E110");
            var Q5;
            Q5=sQuery(id+"F5.wireOp",EDGE,"E112");
            var Q6;
            Q6=sQuery(id+"F5.wireOp",EDGE,"E114");
            var Q7;
            Q7=sQuery(id+"F5.wireOp",EDGE,"E111");
            var Q8;
            Q8=sQuery(id+"F5.wireOp",EDGE,"E113");
            var Q9;
            Q9=sQuery(id+"F5.wireOp",EDGE,"E115");
            var Q10;
            Q10=sQuery(id+"F5.wireOp",EDGE,"E116");
            var Q11;
            Q11=sQuery(id+"F5.wireOp",EDGE,"E119");
            var Q12;
            Q12=sQuery(id+"F5.wireOp",EDGE,"E120");
            var Q13;
            Q13=sQuery(id+"F5.wireOp",EDGE,"E128");
            var Q14;
            Q14=sQuery(id+"F5.wireOp",EDGE,"E127");
            var Q15;
            Q15=sQuery(id+"F5.wireOp",EDGE,"E129");
            var Q16;
            Q16=sQuery(id+"F5.wireOp",EDGE,"E122");
            var Q17;
            Q17=sQuery(id+"F5.wireOp",EDGE,"E126");
            var Q18;
            Q18=sQuery(id+"F5.wireOp",EDGE,"E125");
            var Q19;
            Q19=sQuery(id+"F5.wireOp",EDGE,"E135");
            var Q20;
            Q20=sQuery(id+"F5.wireOp",EDGE,"E134");
            var Q21;
            Q21=sQuery(id+"F5.wireOp",EDGE,"E133");
            var Q22;
            Q22=sQuery(id+"F5.wireOp",EDGE,"E136");
            var Q23;
            Q23=sQuery(id+"F5.wireOp",EDGE,"E137");
            var Q24;
            Q24=sQuery(id+"F5.wireOp",EDGE,"E140");
            var Q25;
            Q25=sQuery(id+"F5.wireOp",EDGE,"E141");
            var Q26;
            Q26=sQuery(id+"F5.wireOp",EDGE,"E144");
            var Q27;
            Q27=sQuery(id+"F5.wireOp",EDGE,"E145");
            var Q28;
            Q28=sQuery(id+"F5.wireOp",EDGE,"E146");
            var Q29;
            Q29=sQuery(id+"F5.wireOp",EDGE,"E147");
            var Q30;
            Q30=sQuery(id+"F5.wireOp",EDGE,"E149");
            var Q31;
            Q31=sQuery(id+"F5.wireOp",EDGE,"E150");
            var Q32;
            Q32=sQuery(id+"F5.wireOp",EDGE,"E151");
            var Q33;
            Q33=sQuery(id+"F5.wireOp",EDGE,"E152");
            var Q34;
            Q34=sQuery(id+"F5.wireOp",EDGE,"E153");
            var Q35;
            Q35=sQuery(id+"F5.wireOp",EDGE,"E143");
            var Q36;
            Q36=sQuery(id+"F5.wireOp",EDGE,"E154");
            var Q37;
            Q37=sQuery(id+"F5.wireOp",EDGE,"E155");
            var Q38;
            Q38=sQuery(id+"F5.wireOp",EDGE,"E157");
            var Q39;
            Q39=sQuery(id+"F5.wireOp",EDGE,"E156");
            var Q40;
            Q40=sQuery(id+"F5.wireOp",EDGE,"E139");
            var Q41;
            Q41=sQuery(id+"F5.wireOp",EDGE,"E138");
            var Q42;
            Q42=sQuery(id+"F5.wireOp",EDGE,"E123");
            var Q43;
            Q43=sQuery(id+"F5.wireOp",EDGE,"E124");
            var Q44;
            Q44=sQuery(id+"F5.wireOp",EDGE,"E117");
            var Q45;
            Q45=sQuery(id+"F5.wireOp",EDGE,"E118");
            var Q46;
            Q46=sQuery(id+"F5.wireOp",EDGE,"E132");
            extrude(context, id + "F6", {"bodyType" : ToolBodyType.SURFACE, "surfaceEntities" : qUnion([Q0, Q1, Q2, Q3, Q4, Q5, Q6, Q7, Q8, Q9, Q10, Q11, Q12, Q13, Q14, Q15, Q16, Q17, Q18, Q19, Q20, Q21, Q22, Q23, Q24, Q25, Q26, Q27, Q28, Q29, Q30, Q31, Q32, Q33, Q34, Q35, Q36, Q37, Q38, Q39, Q40, Q41, Q42, Q43, Q44, Q45, Q46]), "depth" : 6.35 * mm});
        }
        {
            var Q0;
            {var subQ0=sQuery(id+"F5.wireOp",EDGE,"E188");Q0=makeQuery(id+"F5.imprint","IMPRINT",FACE,{"disambiguationData":[TD([[makeQuery(id+"F5.imprint","IMPRINT",EDGE,{"derivedFrom":subQ0}),1.0]])]});}
            var Q1;
            Q1=makeQuery(id+"F5.imprint","IMPRINT",FACE,{"disambiguationData":[TD([[makeQuery(id+"F5.imprint","IMPRINT",EDGE,{"derivedFrom":sQuery(id+"F5.wireOp",EDGE,"E114")}),1.0]])]});
            var Q2;
            Q2=makeQuery(id+"F5.imprint","IMPRINT",FACE,{"disambiguationData":[TD([[makeQuery(id+"F5.imprint","IMPRINT",EDGE,{"derivedFrom":sQuery(id+"F5.wireOp",EDGE,"E111")}),-1.0]])]});
            var Q3;
            Q3=makeQuery(id+"F5.imprint","IMPRINT",FACE,{"disambiguationData":[TD([[makeQuery(id+"F5.imprint","IMPRINT",EDGE,{"derivedFrom":sQuery(id+"F5.wireOp",EDGE,"E119")}),-1.0]])]});
            var Q4;
            {var subQ0=sQuery(id+"F5.wireOp",EDGE,"E187");Q4=makeQuery(id+"F5.imprint","IMPRINT",FACE,{"disambiguationData":[TD([[makeQuery(id+"F5.imprint","IMPRINT",EDGE,{"derivedFrom":subQ0}),1.0]])]});}
            extrude(context, id + "F7", {"entities" : qUnion([Q0, Q1, Q2, Q3, Q4]), "depth" : 6.35 * mm});
        }
        {
            var Q0;
            Q0=makeQuery(id+"F5.imprint","IMPRINT",FACE,{"disambiguationData":[TD([[makeQuery(id+"F5.imprint","IMPRINT",EDGE,{"derivedFrom":sQuery(id+"F5.wireOp",EDGE,"E115")}),-1.0]])]});
            var Q1;
            {var subQ0=sQuery(id+"F5.wireOp",EDGE,"E163");Q1=makeQuery(id+"F5.imprint","IMPRINT",FACE,{"disambiguationData":[TD([[makeQuery(id+"F5.imprint","IMPRINT",EDGE,{"derivedFrom":subQ0}),1.0]])]});}
            extrude(context, id + "F8", {"entities" : qUnion([Q0, Q1]), "depth" : 6.35 * mm});
        }
        {
            var Q0;
            Q0=makeQuery(id+"F5.imprint","IMPRINT",FACE,{"disambiguationData":[TD([[makeQuery(id+"F5.imprint","IMPRINT",EDGE,{"derivedFrom":sQuery(id+"F5.wireOp",EDGE,"E116")}),-1.0]])]});
            var Q1;
            Q1=makeQuery(id+"F5.imprint","IMPRINT",FACE,{"disambiguationData":[TD([[makeQuery(id+"F5.imprint","IMPRINT",EDGE,{"derivedFrom":sQuery(id+"F5.wireOp",EDGE,"E117")}),1.0]])]});
            extrude(context, id + "F9", {"entities" : qUnion([Q0, Q1]), "depth" : 6.35 * mm});
        }
        {
            var Q0;
            Q0=makeQuery(id+"F5.imprint","IMPRINT",FACE,{"disambiguationData":[TD([[makeQuery(id+"F5.imprint","IMPRINT",EDGE,{"derivedFrom":sQuery(id+"F5.wireOp",EDGE,"E127")}),-1.0]])]});
            var Q1;
            Q1=makeQuery(id+"F5.imprint","IMPRINT",FACE,{"disambiguationData":[TD([[makeQuery(id+"F5.imprint","IMPRINT",EDGE,{"derivedFrom":sQuery(id+"F5.wireOp",EDGE,"E128")}),1.0]])]});
            extrude(context, id + "F10", {"entities" : qUnion([Q0, Q1]), "depth" : 6.35 * mm});
        }
        {
            var Q0;
            Q0=makeQuery(id+"F5.imprint","IMPRINT",FACE,{"disambiguationData":[TD([[makeQuery(id+"F5.imprint","IMPRINT",EDGE,{"derivedFrom":sQuery(id+"F5.wireOp",EDGE,"E109")}),-1.0]])]});
            extrude(context, id + "F11", {"entities" : qUnion([Q0]), "operationType" : NewBodyOperationType.REMOVE, "oppositeDirection" : true, "depth" : 50.8 * mm, "hasSecondDirection" : true, "secondDirectionOppositeDirection" : false, "secondDirectionDepth" : 50.8 * mm});
        }
        {
            var Q0;
            Q0=makeQuery(id+"F5.imprint","IMPRINT",FACE,{"disambiguationData":[TD([[makeQuery(id+"F5.imprint","IMPRINT",EDGE,{"derivedFrom":sQuery(id+"F5.wireOp",EDGE,"E107")}),-1.0]])]});
            var Q1;
            Q1=makeQuery(id+"F5.imprint","IMPRINT",FACE,{"disambiguationData":[TD([[makeQuery(id+"F5.imprint","IMPRINT",EDGE,{"derivedFrom":sQuery(id+"F5.wireOp",EDGE,"E140")}),1.0]])]});
            var Q2;
            Q2=makeQuery(id+"F5.imprint","IMPRINT",FACE,{"disambiguationData":[TD([[makeQuery(id+"F5.imprint","IMPRINT",EDGE,{"derivedFrom":sQuery(id+"F5.wireOp",EDGE,"E137")}),1.0]])]});
            var Q3;
            Q3=makeQuery(id+"F5.imprint","IMPRINT",FACE,{"disambiguationData":[TD([[makeQuery(id+"F5.imprint","IMPRINT",EDGE,{"derivedFrom":sQuery(id+"F5.wireOp",EDGE,"E136")}),1.0]])]});
            var Q4;
            Q4=makeQuery(id+"F5.imprint","IMPRINT",FACE,{"disambiguationData":[TD([[makeQuery(id+"F5.imprint","IMPRINT",EDGE,{"derivedFrom":sQuery(id+"F5.wireOp",EDGE,"E133")}),-1.0]])]});
            var Q5;
            Q5=makeQuery(id+"F5.imprint","IMPRINT",FACE,{"disambiguationData":[TD([[makeQuery(id+"F5.imprint","IMPRINT",EDGE,{"derivedFrom":sQuery(id+"F5.wireOp",EDGE,"E135")}),1.0]])]});
            var Q6;
            Q6=makeQuery(id+"F5.imprint","IMPRINT",FACE,{"disambiguationData":[TD([[makeQuery(id+"F5.imprint","IMPRINT",EDGE,{"derivedFrom":sQuery(id+"F5.wireOp",EDGE,"E134")}),-1.0]])]});
            var Q7;
            Q7=makeQuery(id+"F5.imprint","IMPRINT",FACE,{"disambiguationData":[TD([[makeQuery(id+"F5.imprint","IMPRINT",EDGE,{"derivedFrom":sQuery(id+"F5.wireOp",EDGE,"E138")}),-1.0]])]});
            var Q8;
            Q8=makeQuery(id+"F5.imprint","IMPRINT",FACE,{"disambiguationData":[TD([[makeQuery(id+"F5.imprint","IMPRINT",EDGE,{"derivedFrom":sQuery(id+"F5.wireOp",EDGE,"E110")}),-1.0]])]});
            var Q9;
            Q9=makeQuery(id+"F5.imprint","IMPRINT",FACE,{"disambiguationData":[TD([[makeQuery(id+"F5.imprint","IMPRINT",EDGE,{"derivedFrom":sQuery(id+"F5.wireOp",EDGE,"E125")}),1.0]])]});
            var Q10;
            Q10=makeQuery(id+"F5.imprint","IMPRINT",FACE,{"disambiguationData":[TD([[makeQuery(id+"F5.imprint","IMPRINT",EDGE,{"derivedFrom":sQuery(id+"F5.wireOp",EDGE,"E126")}),1.0]])]});
            var Q11;
            Q11=makeQuery(id+"F5.imprint","IMPRINT",FACE,{"disambiguationData":[TD([[makeQuery(id+"F5.imprint","IMPRINT",EDGE,{"derivedFrom":sQuery(id+"F5.wireOp",EDGE,"E132")}),1.0]])]});
            var Q12;
            Q12=makeQuery(id+"F5.imprint","IMPRINT",FACE,{"disambiguationData":[TD([[makeQuery(id+"F5.imprint","IMPRINT",EDGE,{"derivedFrom":sQuery(id+"F5.wireOp",EDGE,"E109")}),-1.0]])]});
            extrude(context, id + "F12", {"entities" : qUnion([Q0, Q1, Q2, Q3, Q4, Q5, Q6, Q7, Q8, Q9, Q10, Q11, Q12]), "depth" : 6.35 * mm});
        }
    });
